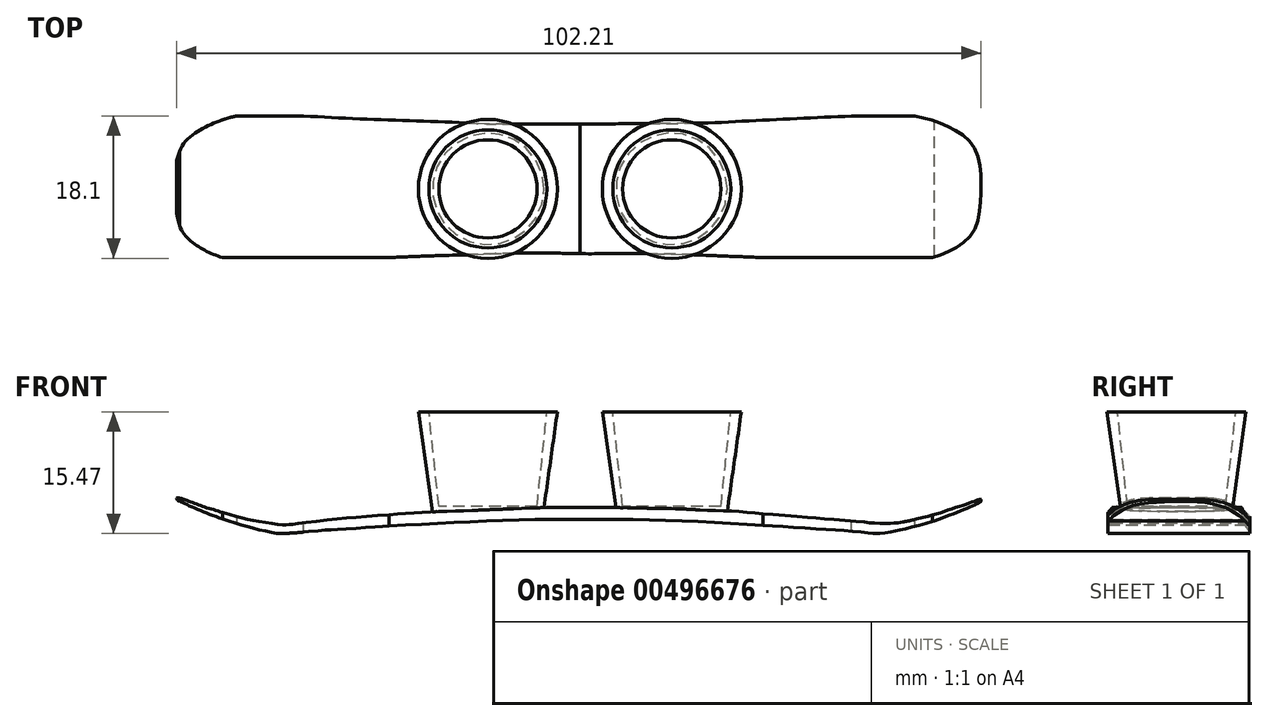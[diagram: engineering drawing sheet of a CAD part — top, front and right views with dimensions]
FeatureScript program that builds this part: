
annotation { "Feature Type Name" : "Feature", "Feature Type Description" : "" }
export const myFeature = defineFeature(function(context is Context, id is Id, definition is map)
    precondition{}
    {
        {
            var Q0;
            Q0=qCreatedBy(makeId("Front.planeOp"),FACE);
            var sketch = newSketch(context, id + "F0", { "sketchPlane" : qUnion([Q0])});
            skFitSpline(sketch, "E0", {"points": [v(-50.87, 5.75) * mm, v(-51.12, 5.77) * mm, v(-51.22, 5.75) * mm, v(-51.2, 5.57) * mm, v(-50.9, 5.38) * mm, v(-50.11, 5) * mm, v(-48.78, 4.42) * mm, v(-47.17, 3.74) * mm, v(-45.53, 3.15) * mm, v(-43.27, 2.4) * mm, v(-41.36, 1.88) * mm, v(-39.1, 1.39) * mm, v(-37.63, 1.25) * mm, v(-33.07, 1.62) * mm, v(-30.76, 1.78) * mm, v(-26.06, 2.07) * mm, v(-23.39, 2.24) * mm, v(-19.33, 2.47) * mm, v(-13.36, 2.77) * mm, v(-7.81, 2.97) * mm, v(0, 3.03) * mm, v(8.25, 2.98) * mm, v(13.08, 2.84) * mm, v(20.36, 2.48) * mm, v(24.98, 2.17) * mm, v(30.63, 1.8) * mm, v(34.56, 1.55) * mm, v(37.01, 1.29) * mm, v(37.55, 1.24) * mm, v(38.3, 1.24) * mm, v(39.86, 1.53) * mm, v(40.8, 1.73) * mm, v(42.86, 2.22) * mm, v(45.03, 2.86) * mm], "startDerivative": vector(-28.18, 2.64) * mm, "endDerivative": vector(73, 22.82) * mm});
            skFitSpline(sketch, "E1", {"points": [v(45.03, 2.86) * mm, v(46.1, 3.25) * mm, v(47.14, 3.64) * mm, v(47.7, 3.85) * mm, v(48.37, 4.1) * mm, v(49.2, 4.47) * mm, v(49.9, 4.76) * mm, v(50.71, 5.18) * mm, v(51, 5.38) * mm, v(51.02, 5.56) * mm, v(50.84, 5.6) * mm, v(50.44, 5.47) * mm, v(49.06, 4.97) * mm, v(46.92, 4.26) * mm, v(45.3, 3.72) * mm, v(44.44, 3.5) * mm, v(43.27, 3.2) * mm, v(41.24, 2.75) * mm, v(40.2, 2.59) * mm, v(39.56, 2.53) * mm, v(38.61, 2.52) * mm, v(37.2, 2.58) * mm, v(36.21, 2.68) * mm, v(31.74, 3.05) * mm, v(28.38, 3.35) * mm, v(23.04, 3.77) * mm, v(21.56, 3.92) * mm, v(19.18, 4.08) * mm, v(15.66, 4.23) * mm, v(11.72, 4.4) * mm, v(8.33, 4.46) * mm, v(5.55, 4.52) * mm, v(2, 4.57) * mm, v(0, 4.57) * mm], "startDerivative": vector(39.96, 14.33) * mm, "endDerivative": vector(-52.54, -0.25) * mm});
            skFitSpline(sketch, "E2", {"points": [v(0, 4.57) * mm, v(-3.54, 4.57) * mm, v(-6.65, 4.45) * mm, v(-10.1, 4.32) * mm, v(-13.17, 4.2) * mm, v(-16.92, 4.07) * mm, v(-19.67, 3.95) * mm, v(-22.52, 3.76) * mm, v(-27.81, 3.36) * mm, v(-32.08, 2.96) * mm, v(-36.07, 2.49) * mm, v(-36.8, 2.4) * mm, v(-37.28, 2.37) * mm, v(-37.87, 2.34) * mm, v(-39.1, 2.5) * mm, v(-41, 2.82) * mm, v(-42.42, 3.1) * mm, v(-44.06, 3.53) * mm, v(-46.26, 4.19) * mm, v(-48, 4.72) * mm, v(-49.66, 5.35) * mm, v(-50.14, 5.52) * mm, v(-50.87, 5.75) * mm], "startDerivative": vector(-61.69, 0.6) * mm, "endDerivative": vector(-29.2, 8.98) * mm});
            skSolve(sketch);
        }
        {
            var Q0;
            Q0 = qSketchRegion(id + "F0", true);
            extrude(context, id + "F1", {"entities" : qUnion([Q0]), "depth" : 18 * mm, "offsetDistance" : 25 * mm});
        }
        {
            var Q0;
            Q0=qCreatedBy(makeId("Top.planeOp"),FACE);
            var sketch = newSketch(context, id + "F2", { "sketchPlane" : qUnion([Q0])});
            skFitSpline(sketch, "E3", {"points": [v(-39.55, 0.42) * mm, v(-42.66, 0.16) * mm, v(-45.5, -0.54) * mm, v(-48.09, -1.7) * mm, v(-49.5, -2.65) * mm, v(-50.43, -3.68) * mm, v(-51.17, -5.43) * mm, v(-51.45, -7.02) * mm, v(-51.42, -11.15) * mm, v(-50.92, -13.7) * mm, v(-50.64, -14.43) * mm, v(-49.8, -15.56) * mm, v(-49, -16.24) * mm, v(-47.64, -17.07) * mm, v(-46.27, -17.7) * mm, v(-43.9, -18.43) * mm, v(-41.78, -18.81) * mm, v(-39.26, -18.85) * mm, v(-36.55, -18.7) * mm, v(-34.22, -18.53) * mm, v(-31.84, -18.35) * mm, v(-29.4, -18.27) * mm, v(-26.73, -18.13) * mm, v(-20.72, -17.85) * mm, v(-15.54, -17.68) * mm, v(-11.55, -17.54) * mm, v(-9.64, -17.48) * mm, v(-6.09, -17.43) * mm, v(-2.92, -17.44) * mm, v(-0.27, -17.5) * mm, v(4.93, -17.5) * mm, v(12.77, -17.6) * mm, v(17.34, -17.77) * mm, v(24.2, -18.04) * mm, v(28.28, -18.23) * mm, v(32.03, -18.45) * mm, v(36.53, -18.8) * mm, v(39.48, -18.9) * mm, v(42.2, -18.63) * mm, v(45.2, -17.86) * mm, v(47.57, -16.85) * mm, v(49.04, -15.81) * mm, v(49.82, -15) * mm, v(50.37, -14) * mm, v(50.66, -12.74) * mm, v(50.86, -11.3) * mm, v(50.97, -7.66) * mm, v(50.78, -6.04) * mm, v(50.45, -4.75) * mm, v(50.01, -3.94) * mm, v(49.48, -3.2) * mm, v(48.94, -2.69) * mm, v(48.24, -2.2) * mm, v(46.74, -1.35) * mm, v(45.33, -0.72) * mm, v(43.13, -0.13) * mm, v(41.57, 0.22) * mm], "startDerivative": vector(-155.76, -8.56) * mm, "endDerivative": vector(-100.62, 22.35) * mm});
            skFitSpline(sketch, "E4", {"points": [v(41.57, 0.22) * mm, v(40.93, 0.3) * mm, v(40.16, 0.37) * mm, v(39.44, 0.4) * mm, v(38.11, 0.35) * mm, v(36.2, 0.14) * mm, v(33.36, -0.07) * mm, v(31.73, -0.14) * mm, v(29.04, -0.26) * mm, v(25.6, -0.43) * mm, v(19.16, -0.76) * mm, v(16.24, -0.89) * mm, v(9.03, -0.97) * mm, v(4.62, -1) * mm, v(-1.07, -1.05) * mm, v(-5.93, -1.04) * mm, v(-10.39, -1.05) * mm, v(-13.25, -0.95) * mm, v(-16.86, -0.79) * mm, v(-21.31, -0.64) * mm, v(-26.7, -0.42) * mm, v(-30.29, -0.27) * mm, v(-32.04, -0.18) * mm, v(-35.12, 0) * mm, v(-35.53, 0.05) * mm, v(-36.01, 0.11) * mm, v(-36.76, 0.19) * mm, v(-37.97, 0.34) * mm, v(-39.55, 0.42) * mm], "startDerivative": vector(-34.56, 5.15) * mm, "endDerivative": vector(-57.7, 1.55) * mm});
            skSolve(sketch);
        }
        {
            var Q0;
            Q0 = qSketchRegion(id + "F2", true);
            extrude(context, id + "F3", {"entities" : qUnion([Q0]), "operationType" : NewBodyOperationType.INTERSECT, "endBound" : BoundingType.SYMMETRIC, "oppositeDirection" : true, "depth" : 25 * mm, "offsetDistance" : 25 * mm});
        }
        {
            var Q0;
            Q0=qCreatedBy(makeId("Top.planeOp"),FACE);
            cPlane(context, id + "F4", {"entities" : qUnion([Q0]), "cplaneType" : CPlaneType.OFFSET, "offset" : 3.7 * mm, "width" : 150 * mm, "height" : 150 * mm});
        }
        {
            var Q0;
            Q0=qCreatedBy(id+"F4.planeOp",FACE);
            var sketch = newSketch(context, id + "F5", { "sketchPlane" : qUnion([Q0])});
            skPoint(sketch, "E5.0", {"position": v(0, -1.04) * mm});
            skPoint(sketch, "E6.0", {"position": v(0, -17.51) * mm});
            skLineSegment(sketch, "E7", {"start": v(0, -1.04) * mm, "end": v(0, -17.51) * mm});
            skCircle(sketch, "E8", {"center": v(11.68, -9.28) * mm, "radius": 7 * mm});
            skPoint(sketch, "E8.centerSnap0", {"position": v(0, -9.28) * mm});
            skCircle(sketch, "E9.MirrorC", {"center": v(-11.68, -9.28) * mm, "radius": 7 * mm});
            skSolve(sketch);
        }
        {
            var Q0;
            Q0 = qSketchRegion(id + "F5", true);
            extrude(context, id + "F6", {"entities" : qUnion([Q0]), "operationType" : NewBodyOperationType.ADD, "depth" : 13 * mm, "offsetDistance" : 25 * mm, "hasDraft" : true, "draftAngle" : 8 * degree});
        }
        {
            var Q0;
            Q0=makeQuery(id+"F6.opExtrude","CAP_FACE",FACE,{"disambiguationData":[OSD([sQuery(id+"F5.wireOp",EDGE,"E9.MirrorC")])],"isStart":false});
            var sketch = newSketch(context, id + "F7", { "sketchPlane" : qUnion([Q0])});
            skCircle(sketch, "E10", {"center": v(-11.68, -9.28) * mm, "radius": 7.5 * mm});
            skSolve(sketch);
        }
        {
            var Q0;
            Q0 = qSketchRegion(id + "F7", true);
            extrude(context, id + "F8", {"entities" : qUnion([Q0]), "operationType" : NewBodyOperationType.REMOVE, "oppositeDirection" : true, "depth" : 12 * mm, "offsetDistance" : 25 * mm, "hasDraft" : true, "draftAngle" : 6 * degree, "draftPullDirection" : true});
        }
        {
            var Q0;
            Q0=makeQuery(id+"F6.opExtrude","CAP_FACE",FACE,{"disambiguationData":[OSD([sQuery(id+"F5.wireOp",EDGE,"E8")])],"isStart":false});
            var sketch = newSketch(context, id + "F9", { "sketchPlane" : qUnion([Q0])});
            skCircle(sketch, "E11", {"center": v(11.68, -9.28) * mm, "radius": 7.5 * mm});
            skSolve(sketch);
        }
        {
            var Q0;
            Q0 = qSketchRegion(id + "F9", true);
            extrude(context, id + "F10", {"entities" : qUnion([Q0]), "operationType" : NewBodyOperationType.REMOVE, "oppositeDirection" : true, "depth" : 12 * mm, "offsetDistance" : 25 * mm, "hasDraft" : true, "draftAngle" : 6 * degree, "draftPullDirection" : true});
        }
    });
